# Revit family: Domotics-DomesticRanges-GEWISS-SYSTEM_SIGNALLING-LAMP_ANTIBLACKOUT_1M
name_source: partatom
category: Apparecchi elettrici
revit_build: Autodesk Revit 2016 (Build: 20161004_0715(x64)
units: mm (PartAtom-declared; Revit-internal decimal feet)

## family parameters
Condiviso = Sì
Host = Superficie
Mantenere orientamento annotazione = Sì
Punto di calcolo locali = Sì
Quota connettore circolare = Usa diametro
Taglio con vuoti quando caricato = No
Tipo di parte = Normale

## types (2) — shared parameters
Autonomy = 1H
Carico apparente = 0 VA
Catalogue = DOMOTICS
Catalogue Range = SYSTEM - DOMESTIC RANGE
Description. = Anti black-out lamp
Duration = 1H
Electrocod = 0781
IDF = 0899e216-8bf0-441b-9677-c45efe73bcf9
IDT = d9da78bc-1723-4630-88d8-a24a365b252f
Immagine tipo = GW21835.jpg
Lamp = LED
Minimum autonomy = 1H
N. poli = 1
No. SYSTEM modules = 1
Produttore = GEWISS S.p.A.
Prospetto di default = 1219 mm
SEO = Lamp
Supply voltage = 230 V ac - 50/60 Hz
Technical sheet = https://www.gewiss.com
Tipo = System Lampade Antiblack-out 1M_GENERICO : GW21835 Lampada anti black-out fissa nero
Type of lamp = LED
URL = https://www.gewiss.com
Version file RFA = 19.4
Volt = 230 V

## per-type parameters (varying)
| type | Colour | Descrizione | EAN code | Modello | Power supply batteries |
| GW20835 - Anti black-out lamp 1module sy/wh | White | ANTI BLACK-OUT LAMP 1MODULE SY/WH | 8011564747579 | GW20835 | Ni-Mh |
| GW21835 - Anti black-out lamp 1module black | Black | ANTI BLACK-OUT LAMP 1MODULE SY/BK | 8011564747586 | GW21835 | Ni - Mh |

## geometry (parser evidence)
native form markers: Sweep x1
no freeform markers — native parametric forms only
